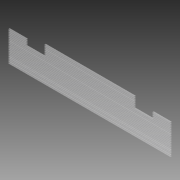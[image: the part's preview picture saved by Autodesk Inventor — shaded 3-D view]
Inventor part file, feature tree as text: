
AUTODESK INVENTOR PART (.ipt)
format: ipt  version: 2012 (Build 160160000, 160)  size: 225,792 bytes
history: native  units: in
note: dims shown in document units (in); Inventor stores cm internally (conversion verified against a paired STEP export)
features: extrude x2, sketch x2
ambient origin geometry x8: Origin, YZ Plane, XZ Plane, XY Plane, X Axis, Y Axis, Z Axis, Center Point
bodies: Solid1 (feature_tree)
feature tree (4):
  extrude  "Extrusion1"  Depth=27.0in
  extrude  "Extrusion2"  Depth=3.0in
  sketch  "Sketch1"  dims[d0=5.0in d1=27.0in]
  sketch  "Sketch2"  dims[d2=0.25in d3=0.0in d4=3.0in d6=3.0in d7=3.0in d8=3.0in d10=1.0in d11=1.75in d12=1.0in d13=0.21in d14=0.23in d15=0.02in d16=0.02in d17=9.0551in d19=0.249in d20=0.3937in d22=1.0in d24=1.0in d25=0.0in]
